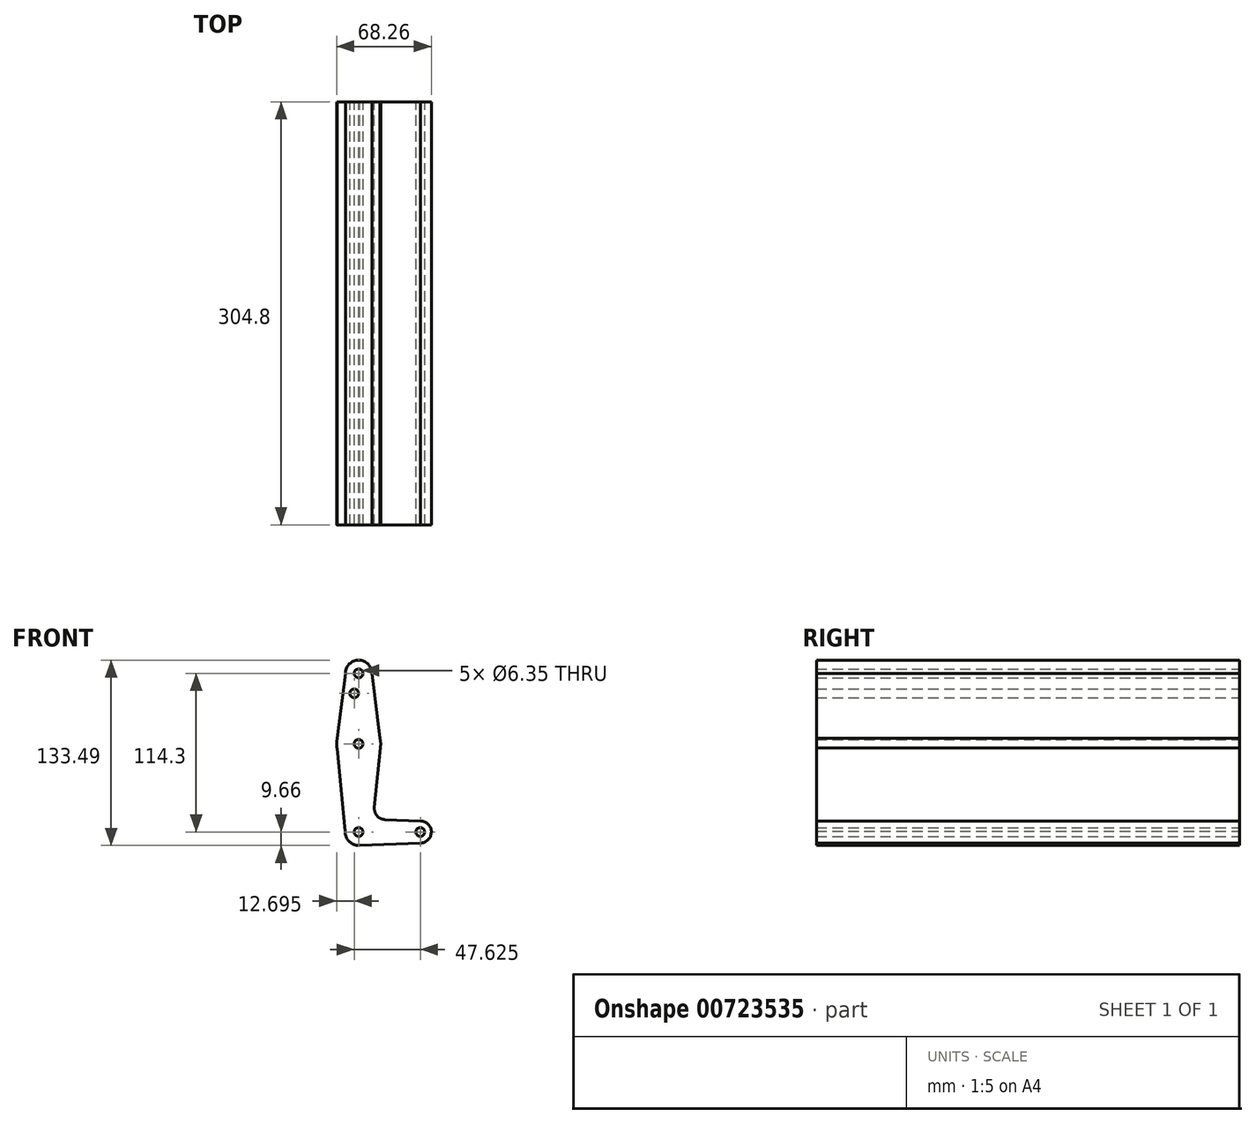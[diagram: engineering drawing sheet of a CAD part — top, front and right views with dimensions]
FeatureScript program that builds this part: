
annotation { "Feature Type Name" : "Feature", "Feature Type Description" : "" }
export const myFeature = defineFeature(function(context is Context, id is Id, definition is map)
    precondition{}
    {
        {
            var Q0;
            Q0=qCreatedBy(makeId("Front.planeOp"),FACE);
            var sketch = newSketch(context, id + "F0", { "sketchPlane" : qUnion([Q0])});
            skLineSegment(sketch, "E0", {"start": v(0, 0) * mm, "end": v(0, 114.3) * mm, "construction": true});
            skLineSegment(sketch, "E1", {"start": v(0, 0) * mm, "end": v(44.45, 0) * mm, "construction": true});
            skCircle(sketch, "E2", {"center": v(0, 114.3) * mm, "radius": 9.53 * mm});
            skCircle(sketch, "E3", {"center": v(0, 63.5) * mm, "radius": 15.88 * mm});
            skLineSegment(sketch, "E4", {"start": v(-9.53, 114.3) * mm, "end": v(-15.88, 63.5) * mm});
            skLineSegment(sketch, "E5", {"start": v(9.53, 114.3) * mm, "end": v(15.88, 63.5) * mm});
            skLineSegment(sketch, "E6", {"start": v(-15.88, 63.5) * mm, "end": v(-9.57, 0) * mm});
            skCircle(sketch, "E7", {"center": v(0, 0) * mm, "radius": 9.66 * mm});
            skLineSegment(sketch, "E8", {"start": v(11.4, 17.65) * mm, "end": v(15.88, 63.5) * mm});
            skCircle(sketch, "E9", {"center": v(44.45, 0) * mm, "radius": 7.94 * mm});
            skLineSegment(sketch, "E10", {"start": v(44.58, 7.94) * mm, "end": v(19, 8.93) * mm});
            skLineSegment(sketch, "E11", {"start": v(0, -9.66) * mm, "end": v(44.45, -7.94) * mm});
            skCircle(sketch, "E12", {"center": v(0, 114.3) * mm, "radius": 3.18 * mm});
            skCircle(sketch, "E13", {"center": v(0, 63.5) * mm, "radius": 3.18 * mm});
            skCircle(sketch, "E14", {"center": v(0, 0) * mm, "radius": 3.18 * mm});
            skCircle(sketch, "E15", {"center": v(44.45, 0) * mm, "radius": 3.18 * mm});
            skCircle(sketch, "E16", {"center": v(-3.18, 99.89) * mm, "radius": 3.18 * mm});
            skArc(sketch, "E17.filletArc", {"start": v(11.4, 17.65) * mm, "mid": v(13.31, 11.65) * mm, "end": v(19, 8.93) * mm});
            skSolve(sketch);
        }
        {
            var Q0;
            Q0 = qSketchRegion(id + "F0", true);
            extrude(context, id + "F1", {"entities" : qUnion([Q0]), "depth" : 304.8 * mm, "offsetDistance" : 25.4 * mm});
        }
    });
